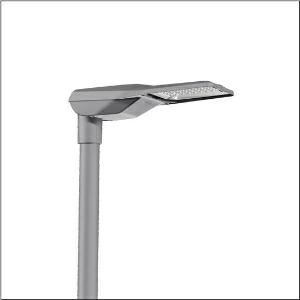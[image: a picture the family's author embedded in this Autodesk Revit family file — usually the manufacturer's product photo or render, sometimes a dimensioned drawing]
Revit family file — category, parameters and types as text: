
# Revit family: streetlight_sl_21_iq_mini___st1_0a_5xe2d41d08gb_4d7e
name_source: partatom
category: Lighting Fixtures
units: mm (PartAtom-declared; Revit-internal decimal feet)

## family parameters
Cut with Voids When Loaded = No
Host = Face
Light Source = No
Part Type = Normal
Room Calculation Point = No
Round Connector Dimension = Use Diameter
Shared = No

## types (1)
- --- (1 x LED, 5920 lm, 37.1 W, 4000K)
    Apparent Load = 37 VA
    CIE Flux Codes = 37 72 97 100 100
    Color Rendering = 70
    Color Temperature = 4000K
    Default Elevation = 1800 mm
    Description = Streetlight SL 21 iQ mini, mast luminaire, primary light control with lens, of PMMA, primary optical cover: cover, of toughened safety glass, transparent, light distribution: ST1.0a, light emission: direct distribution, primary light characteristic: asymmetric, installation type: post-top, side-entry, LED, High Power LED, rated luminous flux: 5.920lm, luminous efficacy: 160lm/W, light colour: 740, colour temperature: 4000K, control: Auto-Match, Temp-Guard, Lumen-Switch, Night-Set, Smart-Wire, Light-Fading, Desk-Remote (wireless, voltage-free reading and setting of iQ features in the workshop via application-optimized NFC function/RFID function), optimised constant luminous flux control (CLO 2.0), presetting dimming linear, mains connection: 220..240V, AC, 50/60Hz, start of lifetime: 37W, end of service life: 39W, reduction: 18W, luminaire housing, of diecast aluminium, powder-coated, Siteco® metallic grey (DB 702S), corrosivity category C5 mid according to DIN EN ISO 12944, please order mast flange separately, inclination adjustable: 0°, 5°, 10°, 15°, sealing non-destructively replaceable, multi-level sealing system, length: 628mm, width: 235mm, height: 110mm, mast flange for spigot size: 42mm (side-entry): 5XC10008XM4, 60/48mm (side-entry/post-top): 5XC10108XM2, 76/60mm (side-entry/post-top): 5XC10108XM1, protection rating (complete): IP66, insulation class (complete): insulation class II (safety insulation), certification: CE, ENEC, ENEC+, VDE, impact resistance: IK09, permissible operating ambient temperature for outdoor applications: -40..+50°C, standard-compliant lighting for roads and squares, packaging unit: 1 piece

Light Distribution: ST1.0a
    Height = 110 mm
    Lamp = 1 x LED
    Lamp Light Flux = 5920 lm
    Lamp Power = 37.1 W
    Lamp count = 1
    Length = 625 mm
    Luminous efficacy = 160 lm/W
    Manufacturer = Siteco
    ModVariant = No
    Model = 5XE2D41D08GB
    Number of Poles = 1
    OnlyDefault = Yes
    Power Factor = 1
    Product Name = Streetlight SL 21 iQ mini | ST1.0a
    Product group = mast luminaire | pylon top
    ProductGroupID = 6100
    Protection Class = Protection class II
    Protection Degree = IP 66
    RLX_Detail_Level = 1
    RLX_Emergency_Light_Flux = 0 lm
    RLX_Emergency_Type = 0
    RLX_Emergency_Type_DB = No
    RlxData = <blob elided: 92277 chars, md5=ba7d9b9f>
    Socket = socket
    Standby Power = 0 W
    System Light Flux = 5920 lm
    System Power = 37 W
    Type Comments = factory setting: luminous flux: 100 % | dim-lin: 254 | 385 mA
    Type Image = l_1003519.jpg
    URL = http://relux.com
    VarID = @adj_122605
    Voltage = 0 V
    Weight = 0.00 kg
    Width = 234 mm

## geometry (parser evidence)
native form markers: Blend x4, Sweep x10
no freeform markers — native parametric forms only
